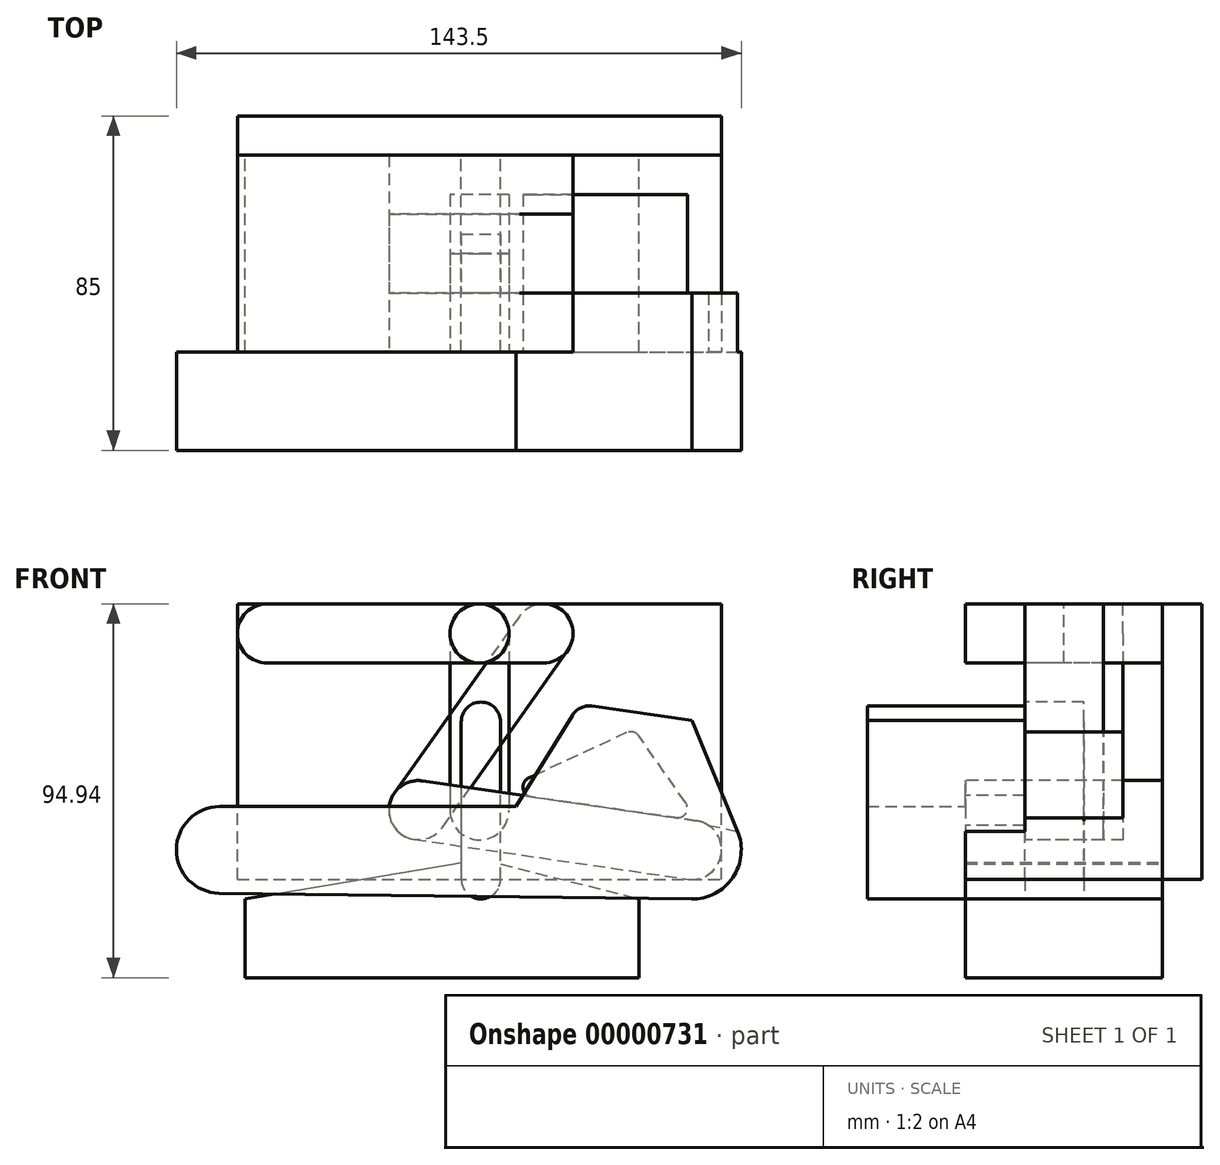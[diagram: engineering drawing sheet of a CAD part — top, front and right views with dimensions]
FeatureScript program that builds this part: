
annotation { "Feature Type Name" : "Feature", "Feature Type Description" : "" }
export const myFeature = defineFeature(function(context is Context, id is Id, definition is map)
    precondition{}
    {
        {
            var Q0;
            Q0=qCreatedBy(makeId("Front.planeOp"),FACE);
            var sketch = newSketch(context, id + "F0", { "sketchPlane" : qUnion([Q0])});
            skLineSegment(sketch, "E0", {"start": v(-54, 27.5) * mm, "end": v(16.26, 27.5) * mm, "construction": true});
            skLineSegment(sketch, "E1", {"start": v(16.26, 27.5) * mm, "end": v(-15.52, -17.39) * mm, "construction": true});
            skLineSegment(sketch, "E2", {"start": v(-15.52, -17.39) * mm, "end": v(54, -27.5) * mm, "construction": true});
            skLineSegment(sketch, "E3", {"start": v(54, 0) * mm, "end": v(-54, 0) * mm, "construction": true});
            skLineSegment(sketch, "E4", {"start": v(-54, 27.5) * mm, "end": v(-54, -27.5) * mm, "construction": true});
            skLineSegment(sketch, "E5", {"start": v(54, -27.5) * mm, "end": v(54, 27.5) * mm, "construction": true});
            skPoint(sketch, "E6", {"position": v(0.37, 5.06) * mm});
            skLineSegment(sketch, "E7", {"start": v(54, -27.5) * mm, "end": v(0, -72.44) * mm, "construction": true});
            skLineSegment(sketch, "E8", {"start": v(-54, 27.5) * mm, "end": v(0, -17.44) * mm, "construction": true});
            skLineSegment(sketch, "E9", {"start": v(0, -17.44) * mm, "end": v(0, -72.44) * mm, "construction": true});
            skPoint(sketch, "E10", {"position": v(0, -44.94) * mm});
            skLineSegment(sketch, "E11", {"start": v(-54, 27.5) * mm, "end": v(10.75, 0.24) * mm});
            skLineSegment(sketch, "E12", {"start": v(10.75, 0.24) * mm, "end": v(-12.72, -49.5) * mm});
            skLineSegment(sketch, "E13", {"start": v(-12.72, -49.5) * mm, "end": v(54, -27.5) * mm});
            skPoint(sketch, "E14", {"position": v(-0.99, -24.63) * mm});
            skLineSegment(sketch, "E15", {"start": v(-15.52, -17.39) * mm, "end": v(-66, -27.5) * mm, "construction": true});
            skLineSegment(sketch, "E16", {"start": v(54, -27.5) * mm, "end": v(-66, -27.5) * mm, "construction": true});
            skLineSegment(sketch, "E17", {"start": v(54, 27.5) * mm, "end": v(-54, 27.5) * mm, "construction": true});
            skLineSegment(sketch, "E18", {"start": v(0, -17.44) * mm, "end": v(0, 27.5) * mm, "construction": true});
            skLineSegment(sketch, "E19", {"start": v(16.26, 27.5) * mm, "end": v(-28.69, 27.5) * mm});
            skLineSegment(sketch, "E20", {"start": v(10.75, 0.24) * mm, "end": v(-24.98, 27.5) * mm});
            skSolve(sketch);
        }
        {
            var Q0;
            Q0=qCreatedBy(makeId("Front.planeOp"),FACE);
            var sketch = newSketch(context, id + "F1", { "sketchPlane" : qUnion([Q0])});
            skCircle(sketch, "E21", {"center": v(54, -27.5) * mm, "radius": 12.5 * mm});
            skCircle(sketch, "E22", {"center": v(-66, -27.5) * mm, "radius": 11 * mm});
            skLineSegment(sketch, "E23", {"start": v(11.07, -13.68) * mm, "end": v(23.6, 6.7) * mm});
            skLineSegment(sketch, "E24", {"start": v(28.58, 9.04) * mm, "end": v(54, 5.34) * mm});
            skLineSegment(sketch, "E25", {"start": v(-66.14, -38.5) * mm, "end": v(53.84, -40) * mm});
            skLineSegment(sketch, "E26", {"start": v(11.07, -13.68) * mm, "end": v(45.18, -18.64) * mm});
            skLineSegment(sketch, "E27", {"start": v(54, 5.34) * mm, "end": v(65.56, -22.74) * mm});
            skCircle(sketch, "E28", {"center": v(54, -27.5) * mm, "radius": 7.5 * mm});
            skArc(sketch, "E29", {"start": v(24.68, 7.94) * mm, "mid": v(8.2, -23.24) * mm, "end": v(18.64, -56.93) * mm, "construction": true});
            skLineSegment(sketch, "E30", {"start": v(-66, -16.5) * mm, "end": v(9.33, -16.5) * mm});
            skLineSegment(sketch, "E31", {"start": v(9.33, -16.5) * mm, "end": v(11.07, -13.68) * mm});
            skArc(sketch, "E32.filletArc", {"start": v(28.58, 9.04) * mm, "mid": v(25.75, 8.62) * mm, "end": v(23.6, 6.7) * mm});
            skLineSegment(sketch, "E33", {"start": v(45.18, -18.64) * mm, "end": v(65.56, -22.74) * mm});
            skSolve(sketch);
        }
        {
            var Q0;
            Q0=qCreatedBy(makeId("Front.planeOp"),FACE);
            var sketch = newSketch(context, id + "F2", { "sketchPlane" : qUnion([Q0])});
            skCircle(sketch, "E34", {"center": v(-54, 27.5) * mm, "radius": 7.5 * mm});
            skCircle(sketch, "E35", {"center": v(16.26, 27.5) * mm, "radius": 7.5 * mm});
            skCircle(sketch, "E36", {"center": v(-15.52, -17.39) * mm, "radius": 7.5 * mm});
            skCircle(sketch, "E37", {"center": v(54, -27.5) * mm, "radius": 7.5 * mm});
            skLineSegment(sketch, "E38", {"start": v(-16.6, -24.81) * mm, "end": v(52.92, -34.92) * mm});
            skLineSegment(sketch, "E39", {"start": v(55.08, -20.08) * mm, "end": v(-14.45, -9.97) * mm});
            skLineSegment(sketch, "E40", {"start": v(-54, 20) * mm, "end": v(16.26, 20) * mm});
            skLineSegment(sketch, "E41", {"start": v(16.26, 35) * mm, "end": v(-54, 35) * mm});
            skSolve(sketch);
        }
        {
            var Q0;
            Q0=qCreatedBy(makeId("Front.planeOp"),FACE);
            var sketch = newSketch(context, id + "F3", { "sketchPlane" : qUnion([Q0])});
            skCircle(sketch, "E42.0", {"center": v(16.26, 27.5) * mm, "radius": 7.5 * mm});
            skCircle(sketch, "E42.1", {"center": v(-15.52, -17.39) * mm, "radius": 7.5 * mm});
            skLineSegment(sketch, "E43", {"start": v(10.14, 31.83) * mm, "end": v(-21.65, -13.05) * mm});
            skLineSegment(sketch, "E44", {"start": v(-9.4, -21.72) * mm, "end": v(22.38, 23.17) * mm});
            skCircle(sketch, "E45", {"center": v(0.37, 5.06) * mm, "radius": 5 * mm});
            skSolve(sketch);
        }
        {
            var Q0;
            Q0=qCreatedBy(makeId("Front.planeOp"),FACE);
            var sketch = newSketch(context, id + "F4", { "sketchPlane" : qUnion([Q0])});
            skLineSegment(sketch, "E46.bottom", {"start": v(-61.5, -35) * mm, "end": v(61.5, -35) * mm});
            skLineSegment(sketch, "E46.top", {"start": v(-61.5, 35) * mm, "end": v(61.5, 35) * mm});
            skLineSegment(sketch, "E46.left", {"start": v(-61.5, -35) * mm, "end": v(-61.5, 35) * mm});
            skLineSegment(sketch, "E46.right", {"start": v(61.5, -35) * mm, "end": v(61.5, 35) * mm});
            skSolve(sketch);
        }
        {
            var Q0;
            Q0=qCreatedBy(makeId("Front.planeOp"),FACE);
            var sketch = newSketch(context, id + "F5", { "sketchPlane" : qUnion([Q0])});
            skCircle(sketch, "E47", {"center": v(0, 27.5) * mm, "radius": 7.5 * mm});
            skCircle(sketch, "E48", {"center": v(0, -17.44) * mm, "radius": 7.5 * mm});
            skLineSegment(sketch, "E49", {"start": v(-7.5, 27.5) * mm, "end": v(-7.5, -17.44) * mm});
            skLineSegment(sketch, "E50", {"start": v(7.5, 27.5) * mm, "end": v(7.5, -17.44) * mm});
            skSolve(sketch);
        }
        {
            var Q0;
            Q0=qCreatedBy(makeId("Front.planeOp"),FACE);
            var sketch = newSketch(context, id + "F6", { "sketchPlane" : qUnion([Q0])});
            skCircle(sketch, "E51", {"center": v(13.55, -11.51) * mm, "radius": 2.5 * mm});
            skLineSegment(sketch, "E52", {"start": v(13.55, -11.51) * mm, "end": v(38.43, 0.03) * mm, "construction": true});
            skLineSegment(sketch, "E53", {"start": v(38.43, 0.03) * mm, "end": v(50.28, -16.85) * mm, "construction": true});
            skLineSegment(sketch, "E54", {"start": v(13.55, -11.51) * mm, "end": v(50.28, -16.85) * mm, "construction": true});
            skCircle(sketch, "E55", {"center": v(11.29, 3.98) * mm, "radius": 2.5 * mm, "construction": true});
            skLineSegment(sketch, "E56", {"start": v(38.43, 0.03) * mm, "end": v(11.29, 3.98) * mm, "construction": true});
            skLineSegment(sketch, "E57", {"start": v(11.29, 3.98) * mm, "end": v(39.12, -20.59) * mm, "construction": true});
            skLineSegment(sketch, "E58", {"start": v(39.12, -20.59) * mm, "end": v(38.43, 0.03) * mm, "construction": true});
            skCircle(sketch, "E59", {"center": v(38.43, 0.03) * mm, "radius": 2.5 * mm});
            skCircle(sketch, "E60", {"center": v(50.28, -16.85) * mm, "radius": 2.5 * mm});
            skLineSegment(sketch, "E61", {"start": v(13.19, -13.98) * mm, "end": v(49.92, -19.33) * mm});
            skLineSegment(sketch, "E62", {"start": v(52.33, -15.42) * mm, "end": v(40.47, 1.46) * mm});
            skLineSegment(sketch, "E63", {"start": v(37.38, 2.3) * mm, "end": v(12.5, -9.24) * mm});
            skArc(sketch, "E64", {"start": v(38.19, -23.1) * mm, "mid": v(45.28, -22.06) * mm, "end": v(51.72, -18.9) * mm, "construction": true});
            skLineSegment(sketch, "E65", {"start": v(9.63, 2.1) * mm, "end": v(38.19, -23.1) * mm, "construction": true});
            skLineSegment(sketch, "E66", {"start": v(14.32, -50.77) * mm, "end": v(49.2, -21.74) * mm, "construction": true});
            skArc(sketch, "E67", {"start": v(8.81, 4.34) * mm, "mid": v(8.81, -4.3) * mm, "end": v(11.28, -12.56) * mm, "construction": true});
            skArc(sketch, "E68", {"start": v(9.27, 5.46) * mm, "mid": v(2.6, -6.4) * mm, "end": v(-0.98, -19.5) * mm, "construction": true});
            skLineSegment(sketch, "E69", {"start": v(11.65, 6.45) * mm, "end": v(38.79, 2.5) * mm, "construction": true});
            skSolve(sketch);
        }
        {
            var Q0;
            Q0=qCreatedBy(makeId("Front.planeOp"),FACE);
            var sketch = newSketch(context, id + "F7", { "sketchPlane" : qUnion([Q0])});
            skCircle(sketch, "E70.0", {"center": v(0.37, 5.06) * mm, "radius": 5 * mm});
            skCircle(sketch, "E71", {"center": v(0.37, -34.94) * mm, "radius": 5 * mm});
            skLineSegment(sketch, "E72.bottom", {"start": v(-59.5, -39.94) * mm, "end": v(40.5, -39.94) * mm});
            skLineSegment(sketch, "E72.top", {"start": v(-59.5, -59.94) * mm, "end": v(40.5, -59.94) * mm});
            skLineSegment(sketch, "E72.left", {"start": v(-59.5, -39.94) * mm, "end": v(-59.5, -59.94) * mm});
            skLineSegment(sketch, "E72.right", {"start": v(40.5, -39.94) * mm, "end": v(40.5, -59.94) * mm});
            skLineSegment(sketch, "E73", {"start": v(-59.5, -39.94) * mm, "end": v(-0.46, -30.01) * mm});
            skLineSegment(sketch, "E74", {"start": v(1.6, -30.1) * mm, "end": v(40.5, -39.94) * mm});
            skLineSegment(sketch, "E75", {"start": v(5.37, -34.94) * mm, "end": v(5.37, 5.06) * mm});
            skLineSegment(sketch, "E76", {"start": v(-4.63, 5.06) * mm, "end": v(-4.63, -34.94) * mm});
            skLineSegment(sketch, "E77", {"start": v(0.37, 5.06) * mm, "end": v(0.37, -34.94) * mm, "construction": true});
            skSolve(sketch);
        }
        {
            var Q0;
            {var subQ0=sQuery(id+"F1.wireOp",EDGE,"E22");var subQ2=makeQuery(id+"F1.imprint","INTERSECT",VERTEX,{"derivedFrom":[subQ0,sQuery(id+"F1.wireOp",EDGE,"E25")]});Q0=makeQuery(id+"F1.imprint","IMPRINT",FACE,{"disambiguationData":[TD([[makeQuery(id+"F1.imprint","IMPRINT",EDGE,{"disambiguationData":[TD([[subQ2,1.0]])],"derivedFrom":subQ0}),1.0]])]});}
            var Q1;
            {var subQ2=sQuery(id+"F1.wireOp",EDGE,"E25");Q1=makeQuery(id+"F1.imprint","IMPRINT",FACE,{"disambiguationData":[TD([[makeQuery(id+"F1.imprint","IMPRINT",EDGE,{"derivedFrom":subQ2}),1.0]])]});}
            var Q2;
            {var subQ0=sQuery(id+"F1.wireOp",EDGE,"E33");var subQ1=sQuery(id+"F1.wireOp",EDGE,"E28");var subQ5=makeQuery(id+"F1.imprint","INTERSECT",VERTEX,{"disambiguationData":[OD(0.0)],"derivedFrom":[subQ1,subQ0]});Q2=makeQuery(id+"F1.imprint","IMPRINT",FACE,{"disambiguationData":[TD([[makeQuery(id+"F1.imprint","IMPRINT",EDGE,{"disambiguationData":[TD([[subQ5,1.0]])],"derivedFrom":subQ1}),-1.0]])]});}
            var Q3;
            Q3=makeQuery(id+"F1.imprint","IMPRINT",FACE,{"disambiguationData":[TD([[makeQuery(id+"F1.imprint","IMPRINT",EDGE,{"derivedFrom":sQuery(id+"F1.wireOp",EDGE,"E23")}),-1.0]])]});
            var Q4;
            {var subQ0=sQuery(id+"F1.wireOp",EDGE,"E33");var subQ1=sQuery(id+"F1.wireOp",EDGE,"E28");var subQ5=makeQuery(id+"F1.imprint","INTERSECT",VERTEX,{"disambiguationData":[OD(0.0)],"derivedFrom":[subQ1,subQ0]});Q4=makeQuery(id+"F1.imprint","IMPRINT",FACE,{"disambiguationData":[TD([[makeQuery(id+"F1.imprint","IMPRINT",EDGE,{"disambiguationData":[TD([[subQ5,1.0]])],"derivedFrom":subQ1}),-1.0]])]});}
            var Q5;
            {var subQ0=sQuery(id+"F1.wireOp",EDGE,"E33");var subQ1=sQuery(id+"F1.wireOp",EDGE,"E28");var subQ5=makeQuery(id+"F1.imprint","INTERSECT",VERTEX,{"disambiguationData":[OD(0.0)],"derivedFrom":[subQ1,subQ0]});Q5=makeQuery(id+"F1.imprint","IMPRINT",FACE,{"disambiguationData":[TD([[makeQuery(id+"F1.imprint","IMPRINT",EDGE,{"disambiguationData":[TD([[subQ5,-1.0]])],"derivedFrom":subQ1}),-1.0]])]});}
            extrude(context, id + "F8", {"entities" : qUnion([Q0, Q1, Q2, Q3, Q4, Q5]), "depth" : 25 * mm});
        }
        {
            var Q0;
            Q0=makeQuery(id+"F1.imprint","IMPRINT",FACE,{"disambiguationData":[TD([[makeQuery(id+"F1.imprint","IMPRINT",EDGE,{"derivedFrom":sQuery(id+"F1.wireOp",EDGE,"E23")}),-1.0]])]});
            var Q1;
            {var subQ0=sQuery(id+"F1.wireOp",EDGE,"E33");var subQ1=sQuery(id+"F1.wireOp",EDGE,"E28");var subQ5=makeQuery(id+"F1.imprint","INTERSECT",VERTEX,{"disambiguationData":[OD(0.0)],"derivedFrom":[subQ1,subQ0]});Q1=makeQuery(id+"F1.imprint","IMPRINT",FACE,{"disambiguationData":[TD([[makeQuery(id+"F1.imprint","IMPRINT",EDGE,{"disambiguationData":[TD([[subQ5,1.0]])],"derivedFrom":subQ1}),-1.0]])]});}
            extrude(context, id + "F9", {"entities" : qUnion([Q0, Q1]), "operationType" : NewBodyOperationType.ADD, "oppositeDirection" : true, "depth" : 15 * mm});
        }
        {
            var Q0;
            {var subQ1=sQuery(id+"F2.wireOp",EDGE,"E38");Q0=makeQuery(id+"F2.imprint","IMPRINT",FACE,{"disambiguationData":[TD([[makeQuery(id+"F2.imprint","IMPRINT",EDGE,{"derivedFrom":subQ1}),1.0]])]});}
            var Q1;
            {var subQ0=sQuery(id+"F2.wireOp",EDGE,"E37");var subQ2=makeQuery(id+"F2.imprint","INTERSECT",VERTEX,{"derivedFrom":[subQ0,sQuery(id+"F2.wireOp",EDGE,"E38")]});Q1=makeQuery(id+"F2.imprint","IMPRINT",FACE,{"disambiguationData":[TD([[makeQuery(id+"F2.imprint","IMPRINT",EDGE,{"disambiguationData":[TD([[subQ2,1.0]])],"derivedFrom":subQ0}),1.0]])]});}
            var Q2;
            {var subQ0=sQuery(id+"F2.wireOp",EDGE,"E36");var subQ2=makeQuery(id+"F2.imprint","INTERSECT",VERTEX,{"derivedFrom":[subQ0,sQuery(id+"F2.wireOp",EDGE,"E38")]});Q2=makeQuery(id+"F2.imprint","IMPRINT",FACE,{"disambiguationData":[TD([[makeQuery(id+"F2.imprint","IMPRINT",EDGE,{"disambiguationData":[TD([[subQ2,1.0]])],"derivedFrom":subQ0}),1.0]])]});}
            var Q3;
            {var subQ0=sQuery(id+"F2.wireOp",EDGE,"E34");var subQ2=makeQuery(id+"F2.imprint","INTERSECT",VERTEX,{"derivedFrom":[subQ0,sQuery(id+"F2.wireOp",EDGE,"E40")]});Q3=makeQuery(id+"F2.imprint","IMPRINT",FACE,{"disambiguationData":[TD([[makeQuery(id+"F2.imprint","IMPRINT",EDGE,{"disambiguationData":[TD([[subQ2,1.0]])],"derivedFrom":subQ0}),1.0]])]});}
            var Q4;
            {var subQ1=sQuery(id+"F2.wireOp",EDGE,"E40");Q4=makeQuery(id+"F2.imprint","IMPRINT",FACE,{"disambiguationData":[TD([[makeQuery(id+"F2.imprint","IMPRINT",EDGE,{"derivedFrom":subQ1}),1.0]])]});}
            var Q5;
            {var subQ0=sQuery(id+"F2.wireOp",EDGE,"E35");var subQ2=makeQuery(id+"F2.imprint","INTERSECT",VERTEX,{"derivedFrom":[subQ0,sQuery(id+"F2.wireOp",EDGE,"E40")]});Q5=makeQuery(id+"F2.imprint","IMPRINT",FACE,{"disambiguationData":[TD([[makeQuery(id+"F2.imprint","IMPRINT",EDGE,{"disambiguationData":[TD([[subQ2,1.0]])],"derivedFrom":subQ0}),1.0]])]});}
            extrude(context, id + "F10", {"entities" : qUnion([Q0, Q1, Q2, Q3, Q4, Q5]), "oppositeDirection" : true, "depth" : 50 * mm});
        }
        {
            var Q0;
            {var subQ0=sQuery(id+"F2.wireOp",EDGE,"E37");var subQ2=makeQuery(id+"F2.imprint","INTERSECT",VERTEX,{"derivedFrom":[subQ0,sQuery(id+"F2.wireOp",EDGE,"E38")]});Q0=makeQuery(id+"F2.imprint","IMPRINT",FACE,{"disambiguationData":[TD([[makeQuery(id+"F2.imprint","IMPRINT",EDGE,{"disambiguationData":[TD([[subQ2,1.0]])],"derivedFrom":subQ0}),1.0]])]});}
            extrude(context, id + "F11", {"entities" : qUnion([Q0]), "operationType" : NewBodyOperationType.ADD, "depth" : 25 * mm});
        }
        {
            var Q0;
            {var subQ0=sQuery(id+"F3.wireOp",EDGE,"E42.1");var subQ2=makeQuery(id+"F3.imprint","INTERSECT",VERTEX,{"derivedFrom":[subQ0,sQuery(id+"F3.wireOp",EDGE,"E43")]});Q0=makeQuery(id+"F3.imprint","IMPRINT",FACE,{"disambiguationData":[TD([[makeQuery(id+"F3.imprint","IMPRINT",EDGE,{"disambiguationData":[TD([[subQ2,-1.0]])],"derivedFrom":subQ0}),1.0]])]});}
            var Q1;
            {var subQ1=sQuery(id+"F3.wireOp",EDGE,"E43");Q1=makeQuery(id+"F3.imprint","IMPRINT",FACE,{"disambiguationData":[TD([[makeQuery(id+"F3.imprint","IMPRINT",EDGE,{"derivedFrom":subQ1}),1.0]])]});}
            var Q2;
            Q2=makeQuery(id+"F3.imprint","IMPRINT",FACE,{"disambiguationData":[TD([[makeQuery(id+"F3.imprint","IMPRINT",EDGE,{"derivedFrom":sQuery(id+"F3.wireOp",EDGE,"E45")}),1.0]])]});
            var Q3;
            {var subQ0=sQuery(id+"F3.wireOp",EDGE,"E42.0");var subQ2=makeQuery(id+"F3.imprint","INTERSECT",VERTEX,{"derivedFrom":[subQ0,sQuery(id+"F3.wireOp",EDGE,"E43")]});Q3=makeQuery(id+"F3.imprint","IMPRINT",FACE,{"disambiguationData":[TD([[makeQuery(id+"F3.imprint","IMPRINT",EDGE,{"disambiguationData":[TD([[subQ2,-1.0]])],"derivedFrom":subQ0}),1.0]])]});}
            extrude(context, id + "F12", {"entities" : qUnion([Q0, Q1, Q2, Q3]), "oppositeDirection" : true, "depth" : 20 * mm});
        }
        {
            var Q0;
            Q0=makeQuery(id+"F4.imprint","IMPRINT",FACE,{"disambiguationData":[TD([[makeQuery(id+"F4.imprint","IMPRINT",EDGE,{"derivedFrom":sQuery(id+"F4.wireOp",EDGE,"E46.bottom")}),1.0]])]});
            extrude(context, id + "F13", {"entities" : qUnion([Q0]), "oppositeDirection" : true, "depth" : 10 * mm});
        }
        {
            var Q0;
            {var subQ0=sQuery(id+"F5.wireOp",EDGE,"E47");var subQ2=makeQuery(id+"F5.imprint","INTERSECT",VERTEX,{"derivedFrom":[subQ0,sQuery(id+"F5.wireOp",EDGE,"E49")]});Q0=makeQuery(id+"F5.imprint","IMPRINT",FACE,{"disambiguationData":[TD([[makeQuery(id+"F5.imprint","IMPRINT",EDGE,{"disambiguationData":[TD([[subQ2,1.0]])],"derivedFrom":subQ0}),1.0]])]});}
            var Q1;
            {var subQ1=sQuery(id+"F5.wireOp",EDGE,"E49");Q1=makeQuery(id+"F5.imprint","IMPRINT",FACE,{"disambiguationData":[TD([[makeQuery(id+"F5.imprint","IMPRINT",EDGE,{"derivedFrom":subQ1}),1.0]])]});}
            var Q2;
            {var subQ0=sQuery(id+"F5.wireOp",EDGE,"E48");var subQ2=makeQuery(id+"F5.imprint","INTERSECT",VERTEX,{"derivedFrom":[subQ0,sQuery(id+"F5.wireOp",EDGE,"E49")]});Q2=makeQuery(id+"F5.imprint","IMPRINT",FACE,{"disambiguationData":[TD([[makeQuery(id+"F5.imprint","IMPRINT",EDGE,{"disambiguationData":[TD([[subQ2,1.0]])],"derivedFrom":subQ0}),1.0]])]});}
            extrude(context, id + "F14", {"entities" : qUnion([Q0, Q1, Q2]), "oppositeDirection" : true, "depth" : 25 * mm});
        }
        {
            var Q0;
            {var subQ0=sQuery(id+"F5.wireOp",EDGE,"E47");var subQ2=makeQuery(id+"F5.imprint","INTERSECT",VERTEX,{"derivedFrom":[subQ0,sQuery(id+"F5.wireOp",EDGE,"E49")]});Q0=makeQuery(id+"F5.imprint","IMPRINT",FACE,{"disambiguationData":[TD([[makeQuery(id+"F5.imprint","IMPRINT",EDGE,{"disambiguationData":[TD([[subQ2,1.0]])],"derivedFrom":subQ0}),1.0]])]});}
            extrude(context, id + "F15", {"entities" : qUnion([Q0]), "oppositeDirection" : true, "depth" : 25 * mm});
        }
        {
            var Q0;
            {var subQ0=sQuery(id+"F6.wireOp",EDGE,"E51");var subQ3=sQuery(id+"F6.wireOp",EDGE,"E61");var subQ4=makeQuery(id+"F6.imprint","INTERSECT",VERTEX,{"derivedFrom":[subQ0,subQ3]});var subQ6=sQuery(id+"F6.wireOp",EDGE,"E59");var subQ8=sQuery(id+"F6.wireOp",EDGE,"E62");var subQ9=makeQuery(id+"F6.imprint","INTERSECT",VERTEX,{"derivedFrom":[subQ6,subQ8]});var subQ11=sQuery(id+"F6.wireOp",EDGE,"E60");var subQ13=makeQuery(id+"F6.imprint","INTERSECT",VERTEX,{"derivedFrom":[subQ11,subQ3]});var subQ14=makeQuery(id+"F6.imprint","IMPRINT",EDGE,{"disambiguationData":[TD([[subQ13,1.0]])],"derivedFrom":subQ11});Q0=qUnion([makeQuery(id+"F6.imprint","IMPRINT",FACE,{"disambiguationData":[TD([[makeQuery(id+"F6.imprint","IMPRINT",EDGE,{"disambiguationData":[TD([[subQ4,1.0]])],"derivedFrom":subQ0}),1.0]])]}),makeQuery(id+"F6.imprint","IMPRINT",FACE,{"disambiguationData":[TD([[makeQuery(id+"F6.imprint","IMPRINT",EDGE,{"disambiguationData":[TD([[subQ9,-1.0]])],"derivedFrom":subQ6}),1.0]])]}),makeQuery(id+"F6.imprint","IMPRINT",FACE,{"disambiguationData":[TD([[subQ14,1.0]])]}),makeQuery(id+"F6.imprint","IMPRINT",FACE,{"disambiguationData":[TD([[makeQuery(id+"F6.imprint","IMPRINT",EDGE,{"derivedFrom":subQ3}),1.0]])]})]);}
            extrude(context, id + "F16", {"entities" : qUnion([Q0]), "oppositeDirection" : true, "depth" : 25 * mm});
        }
        {
            var Q0;
            {var subQ0=sQuery(id+"F7.wireOp",EDGE,"E71");var subQ5=makeQuery(id+"F7.imprint","INTERSECT",VERTEX,{"derivedFrom":[subQ0,sQuery(id+"F7.wireOp",EDGE,"E74")]});Q0=makeQuery(id+"F7.imprint","IMPRINT",FACE,{"disambiguationData":[TD([[makeQuery(id+"F7.imprint","IMPRINT",EDGE,{"disambiguationData":[TD([[subQ5,1.0]])],"derivedFrom":subQ0}),1.0]])]});}
            var Q1;
            {var subQ1=sQuery(id+"F7.wireOp",EDGE,"E74");var subQ3=sQuery(id+"F7.wireOp",EDGE,"E71");var subQ5=makeQuery(id+"F7.imprint","INTERSECT",VERTEX,{"derivedFrom":[subQ3,subQ1]});Q1=makeQuery(id+"F7.imprint","IMPRINT",FACE,{"disambiguationData":[TD([[makeQuery(id+"F7.imprint","IMPRINT",EDGE,{"disambiguationData":[TD([[subQ5,1.0]])],"derivedFrom":subQ3}),-1.0]])]});}
            var Q2;
            {var subQ1=sQuery(id+"F7.wireOp",EDGE,"E73");var subQ3=sQuery(id+"F7.wireOp",EDGE,"E71");var subQ5=makeQuery(id+"F7.imprint","INTERSECT",VERTEX,{"derivedFrom":[subQ3,subQ1]});Q2=makeQuery(id+"F7.imprint","IMPRINT",FACE,{"disambiguationData":[TD([[makeQuery(id+"F7.imprint","IMPRINT",EDGE,{"disambiguationData":[TD([[subQ5,-1.0]])],"derivedFrom":subQ3}),-1.0]])]});}
            var Q3;
            {var subQ3=sQuery(id+"F7.wireOp",EDGE,"E70.0");var subQ5=sQuery(id+"F7.wireOp",EDGE,"E75");var subQ8=makeQuery(id+"F7.imprint","INTERSECT",VERTEX,{"derivedFrom":[subQ3,subQ5]});Q3=makeQuery(id+"F7.imprint","IMPRINT",FACE,{"disambiguationData":[TD([[makeQuery(id+"F7.imprint","IMPRINT",EDGE,{"disambiguationData":[TD([[subQ8,1.0]])],"derivedFrom":subQ3}),-1.0]])]});}
            var Q4;
            {var subQ0=sQuery(id+"F7.wireOp",EDGE,"E70.0");var subQ2=makeQuery(id+"F7.imprint","INTERSECT",VERTEX,{"derivedFrom":[subQ0,sQuery(id+"F7.wireOp",EDGE,"E75")]});Q4=makeQuery(id+"F7.imprint","IMPRINT",FACE,{"disambiguationData":[TD([[makeQuery(id+"F7.imprint","IMPRINT",EDGE,{"disambiguationData":[TD([[subQ2,-1.0]])],"derivedFrom":subQ0}),1.0]])]});}
            extrude(context, id + "F17", {"entities" : qUnion([Q0, Q1, Q2, Q3, Q4]), "oppositeDirection" : true, "depth" : 15 * mm});
        }
        {
            var Q0;
            {var subQ0=sQuery(id+"F7.wireOp",EDGE,"E76");var subQ3=sQuery(id+"F7.wireOp",EDGE,"E71");var subQ4=makeQuery(id+"F7.imprint","INTERSECT",VERTEX,{"derivedFrom":[subQ3,subQ0]});Q0=makeQuery(id+"F7.imprint","IMPRINT",FACE,{"disambiguationData":[TD([[makeQuery(id+"F7.imprint","IMPRINT",EDGE,{"disambiguationData":[TD([[subQ4,-1.0]])],"derivedFrom":subQ3}),-1.0]])]});}
            var Q1;
            Q1=makeQuery(id+"F7.imprint","IMPRINT",FACE,{"disambiguationData":[TD([[makeQuery(id+"F7.imprint","IMPRINT",EDGE,{"derivedFrom":sQuery(id+"F7.wireOp",EDGE,"E72.top")}),1.0]])]});
            var Q2;
            {var subQ0=sQuery(id+"F7.wireOp",EDGE,"E75");var subQ3=sQuery(id+"F7.wireOp",EDGE,"E71");var subQ4=makeQuery(id+"F7.imprint","INTERSECT",VERTEX,{"derivedFrom":[subQ3,subQ0]});Q2=makeQuery(id+"F7.imprint","IMPRINT",FACE,{"disambiguationData":[TD([[makeQuery(id+"F7.imprint","IMPRINT",EDGE,{"disambiguationData":[TD([[subQ4,1.0]])],"derivedFrom":subQ3}),-1.0]])]});}
            extrude(context, id + "F18", {"entities" : qUnion([Q0, Q1, Q2]), "depth" : 50 * mm});
        }
        {
            var Q0;
            Q0=makeQuery(id+"F12.opExtrude","SWEPT_BODY",BODY,{"disambiguationData":[OSD([sQuery(id+"F3.wireOp",EDGE,"E42.0"),sQuery(id+"F3.wireOp",EDGE,"E42.1"),sQuery(id+"F3.wireOp",EDGE,"E43"),sQuery(id+"F3.wireOp",EDGE,"E44")])]});
            var Q1;
            Q1=makeQuery(id+"F14.opExtrude","SWEPT_BODY",BODY,{"disambiguationData":[OSD([sQuery(id+"F5.wireOp",EDGE,"E47"),sQuery(id+"F5.wireOp",EDGE,"E48"),sQuery(id+"F5.wireOp",EDGE,"E49"),sQuery(id+"F5.wireOp",EDGE,"E50")])]});
            var Q2;
            Q2=makeQuery(id+"F16.opExtrude","SWEPT_BODY",BODY,{"disambiguationData":[OSD([sQuery(id+"F6.wireOp",EDGE,"E51"),sQuery(id+"F6.wireOp",EDGE,"E59"),sQuery(id+"F6.wireOp",EDGE,"E60"),sQuery(id+"F6.wireOp",EDGE,"E61"),sQuery(id+"F6.wireOp",EDGE,"E62"),sQuery(id+"F6.wireOp",EDGE,"E63")])]});
            var Q3;
            Q3=makeQuery(id+"F17.opExtrude","SWEPT_BODY",BODY,{"disambiguationData":[OSD([sQuery(id+"F7.wireOp",EDGE,"E70.0"),sQuery(id+"F7.wireOp",EDGE,"E71"),sQuery(id+"F7.wireOp",EDGE,"E75"),sQuery(id+"F7.wireOp",EDGE,"E76")])]});
            transform(context, id + "F19", {"entities" : qUnion([Q0, Q1, Q2, Q3]), "transformType" : TransformType.TRANSLATION_3D, "dx" : 0 * mm, "dy" : 15 * mm, "dz" : 0 * mm, "makeCopy" : false});
        }
        {
            var Q0;
            Q0=makeQuery(id+"F13.opExtrude","SWEPT_BODY",BODY,{"disambiguationData":[OSD([sQuery(id+"F4.wireOp",EDGE,"E46.bottom"),sQuery(id+"F4.wireOp",EDGE,"E46.top"),sQuery(id+"F4.wireOp",EDGE,"E46.left"),sQuery(id+"F4.wireOp",EDGE,"E46.right")])]});
            var Q1;
            Q1=makeQuery(id+"F18.opExtrude","SWEPT_BODY",BODY,{"disambiguationData":[OSD([sQuery(id+"F7.wireOp",EDGE,"E71"),sQuery(id+"F7.wireOp",EDGE,"E72.top"),sQuery(id+"F7.wireOp",EDGE,"E72.left"),sQuery(id+"F7.wireOp",EDGE,"E72.right"),sQuery(id+"F7.wireOp",EDGE,"E73"),sQuery(id+"F7.wireOp",EDGE,"E74"),sQuery(id+"F7.wireOp",EDGE,"E75"),sQuery(id+"F7.wireOp",EDGE,"E76")])]});
            transform(context, id + "F20", {"entities" : qUnion([Q0, Q1]), "transformType" : TransformType.TRANSLATION_3D, "dx" : 0 * mm, "dy" : 50 * mm, "dz" : 0 * mm, "makeCopy" : false});
        }
    });
